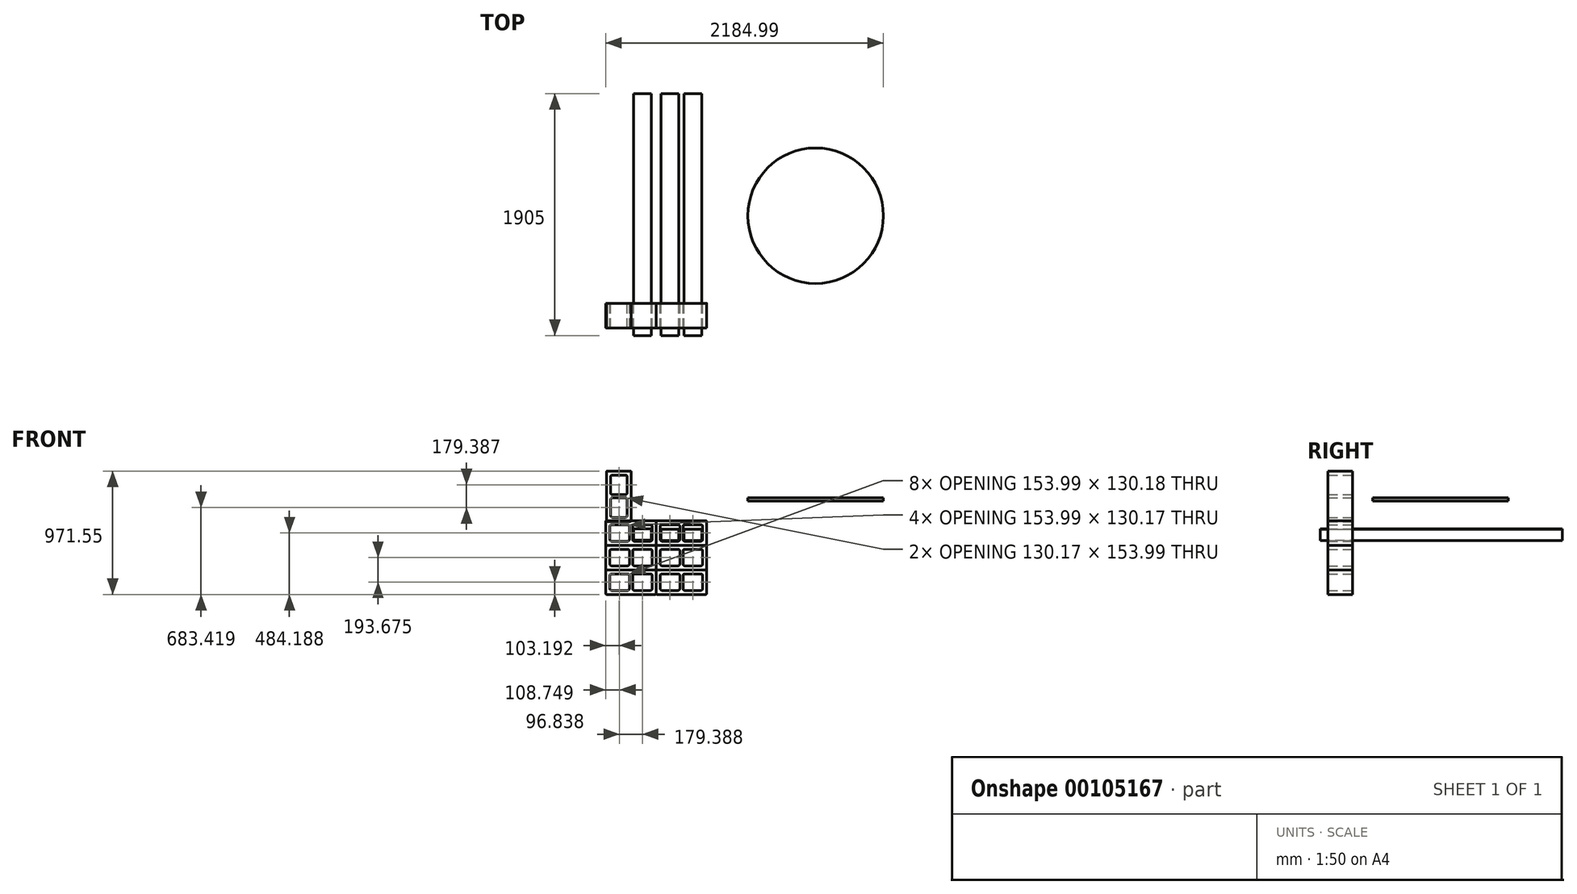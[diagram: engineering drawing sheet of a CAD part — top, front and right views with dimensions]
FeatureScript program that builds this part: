
annotation { "Feature Type Name" : "Feature", "Feature Type Description" : "" }
export const myFeature = defineFeature(function(context is Context, id is Id, definition is map)
    precondition{}
    {
        {
            var Q0;
            Q0=qCreatedBy(makeId("Front.planeOp"),FACE);
            var sketch = newSketch(context, id + "F0", { "sketchPlane" : qUnion([Q0])});
            skLineSegment(sketch, "E0.bottom", {"start": v(-6.35, 0) * mm, "end": v(-390.53, 0) * mm});
            skLineSegment(sketch, "E0.top", {"start": v(-6.35, 193.68) * mm, "end": v(-390.53, 193.67) * mm});
            skLineSegment(sketch, "E0.left", {"start": v(0, 6.35) * mm, "end": v(0, 187.32) * mm});
            skLineSegment(sketch, "E0.right", {"start": v(-396.88, 6.35) * mm, "end": v(-396.88, 187.32) * mm});
            skLineSegment(sketch, "E1.bottom", {"start": v(-352.43, 161.92) * mm, "end": v(-223.84, 161.92) * mm});
            skLineSegment(sketch, "E1.top", {"start": v(-352.43, 31.75) * mm, "end": v(-223.84, 31.75) * mm});
            skLineSegment(sketch, "E1.left", {"start": v(-365.13, 149.22) * mm, "end": v(-365.13, 44.45) * mm});
            skLineSegment(sketch, "E1.right", {"start": v(-211.14, 149.23) * mm, "end": v(-211.14, 44.45) * mm});
            skLineSegment(sketch, "E2.bottom", {"start": v(-173.04, 161.93) * mm, "end": v(-44.45, 161.93) * mm});
            skLineSegment(sketch, "E2.top", {"start": v(-173.04, 31.75) * mm, "end": v(-44.45, 31.75) * mm});
            skLineSegment(sketch, "E2.left", {"start": v(-185.74, 149.23) * mm, "end": v(-185.74, 44.45) * mm});
            skLineSegment(sketch, "E2.right", {"start": v(-31.75, 149.23) * mm, "end": v(-31.75, 44.45) * mm});
            skPoint(sketch, "E3.visualSharp", {"position": v(-396.88, 193.67) * mm});
            skArc(sketch, "E3.filletArc", {"start": v(-390.53, 193.67) * mm, "mid": v(-395.02, 191.82) * mm, "end": v(-396.88, 187.32) * mm});
            skPoint(sketch, "E4.visualSharp", {"position": v(-396.88, 0) * mm});
            skArc(sketch, "E4.filletArc", {"start": v(-396.88, 6.35) * mm, "mid": v(-395.02, 1.86) * mm, "end": v(-390.53, 0) * mm});
            skPoint(sketch, "E5.visualSharp", {"position": v(0, 0) * mm});
            skArc(sketch, "E5.filletArc", {"start": v(-6.35, 0) * mm, "mid": v(-1.86, 1.86) * mm, "end": v(0, 6.35) * mm});
            skPoint(sketch, "E6.visualSharp", {"position": v(0, 193.68) * mm});
            skArc(sketch, "E6.filletArc", {"start": v(0, 187.32) * mm, "mid": v(-1.86, 191.82) * mm, "end": v(-6.35, 193.67) * mm});
            skPoint(sketch, "E7.visualSharp", {"position": v(-365.13, 161.92) * mm});
            skArc(sketch, "E7.filletArc", {"start": v(-352.43, 161.92) * mm, "mid": v(-361.4, 158.2) * mm, "end": v(-365.13, 149.22) * mm});
            skPoint(sketch, "E8.visualSharp", {"position": v(-365.13, 31.75) * mm});
            skArc(sketch, "E8.filletArc", {"start": v(-365.13, 44.45) * mm, "mid": v(-361.4, 35.47) * mm, "end": v(-352.43, 31.75) * mm});
            skPoint(sketch, "E9.visualSharp", {"position": v(-211.14, 31.75) * mm});
            skArc(sketch, "E9.filletArc", {"start": v(-223.84, 31.75) * mm, "mid": v(-214.86, 35.47) * mm, "end": v(-211.14, 44.45) * mm});
            skPoint(sketch, "E10.visualSharp", {"position": v(-211.14, 161.92) * mm});
            skArc(sketch, "E10.filletArc", {"start": v(-211.14, 149.23) * mm, "mid": v(-214.86, 158.2) * mm, "end": v(-223.84, 161.93) * mm});
            skPoint(sketch, "E11.visualSharp", {"position": v(-185.74, 161.93) * mm});
            skArc(sketch, "E11.filletArc", {"start": v(-173.04, 161.93) * mm, "mid": v(-182.02, 158.2) * mm, "end": v(-185.74, 149.23) * mm});
            skPoint(sketch, "E12.visualSharp", {"position": v(-185.74, 31.75) * mm});
            skArc(sketch, "E12.filletArc", {"start": v(-185.74, 44.45) * mm, "mid": v(-182.02, 35.47) * mm, "end": v(-173.04, 31.75) * mm});
            skPoint(sketch, "E13.visualSharp", {"position": v(-31.75, 31.75) * mm});
            skArc(sketch, "E13.filletArc", {"start": v(-44.45, 31.75) * mm, "mid": v(-35.47, 35.47) * mm, "end": v(-31.75, 44.45) * mm});
            skPoint(sketch, "E14.visualSharp", {"position": v(-31.75, 161.93) * mm});
            skArc(sketch, "E14.filletArc", {"start": v(-31.75, 149.23) * mm, "mid": v(-35.47, 158.2) * mm, "end": v(-44.45, 161.93) * mm});
            skSolve(sketch);
        }
        {
            var Q0;
            Q0=qCreatedBy(makeId("Top.planeOp"),FACE);
            cPlane(context, id + "F1", {"entities" : qUnion([Q0]), "cplaneType" : CPlaneType.OFFSET, "offset" : 736.6 * mm, "width" : 152.4 * mm, "height" : 152.4 * mm});
        }
        {
            var Q0;
            Q0 = qSketchRegion(id + "F0", true);
            extrude(context, id + "F2", {"entities" : qUnion([Q0]), "depth" : 193.67 * mm});
        }
        {
            var Q0;
            Q0=makeQuery(id+"F2.opExtrude","SWEPT_BODY",BODY,{"disambiguationData":[OSD([sQuery(id+"F0.wireOp",EDGE,"E0.bottom"),sQuery(id+"F0.wireOp",EDGE,"E0.top"),sQuery(id+"F0.wireOp",EDGE,"E0.left"),sQuery(id+"F0.wireOp",EDGE,"E0.right"),sQuery(id+"F0.wireOp",EDGE,"E1.bottom"),sQuery(id+"F0.wireOp",EDGE,"E1.top"),sQuery(id+"F0.wireOp",EDGE,"E1.left"),sQuery(id+"F0.wireOp",EDGE,"E1.right"),sQuery(id+"F0.wireOp",EDGE,"E2.bottom"),sQuery(id+"F0.wireOp",EDGE,"E2.top"),sQuery(id+"F0.wireOp",EDGE,"E2.left"),sQuery(id+"F0.wireOp",EDGE,"E2.right"),sQuery(id+"F0.wireOp",EDGE,"E3.filletArc"),sQuery(id+"F0.wireOp",EDGE,"E4.filletArc"),sQuery(id+"F0.wireOp",EDGE,"E5.filletArc"),sQuery(id+"F0.wireOp",EDGE,"E6.filletArc"),sQuery(id+"F0.wireOp",EDGE,"E7.filletArc"),sQuery(id+"F0.wireOp",EDGE,"E8.filletArc"),sQuery(id+"F0.wireOp",EDGE,"E9.filletArc"),sQuery(id+"F0.wireOp",EDGE,"E10.filletArc"),sQuery(id+"F0.wireOp",EDGE,"E11.filletArc"),sQuery(id+"F0.wireOp",EDGE,"E12.filletArc"),sQuery(id+"F0.wireOp",EDGE,"E13.filletArc"),sQuery(id+"F0.wireOp",EDGE,"E14.filletArc")])]});
            transform(context, id + "F3", {"entities" : qUnion([Q0]), "transformType" : TransformType.TRANSLATION_3D, "dx" : 396.88 * mm, "dy" : 0 * mm, "dz" : 0 * mm, "makeCopy" : true});
        }
        {
            var Q0;
            Q0=qCreatedBy(id+"F1.planeOp",FACE);
            var sketch = newSketch(context, id + "F4", { "sketchPlane" : qUnion([Q0])});
            skCircle(sketch, "E15", {"center": v(1254.71, 689.64) * mm, "radius": 533.4 * mm});
            skSolve(sketch);
        }
        {
            var Q0;
            Q0=makeQuery(id+"F2.opExtrude","SWEPT_BODY",BODY,{"disambiguationData":[OSD([sQuery(id+"F0.wireOp",EDGE,"E0.bottom"),sQuery(id+"F0.wireOp",EDGE,"E0.top"),sQuery(id+"F0.wireOp",EDGE,"E0.left"),sQuery(id+"F0.wireOp",EDGE,"E0.right"),sQuery(id+"F0.wireOp",EDGE,"E1.bottom"),sQuery(id+"F0.wireOp",EDGE,"E1.top"),sQuery(id+"F0.wireOp",EDGE,"E1.left"),sQuery(id+"F0.wireOp",EDGE,"E1.right"),sQuery(id+"F0.wireOp",EDGE,"E2.bottom"),sQuery(id+"F0.wireOp",EDGE,"E2.top"),sQuery(id+"F0.wireOp",EDGE,"E2.left"),sQuery(id+"F0.wireOp",EDGE,"E2.right"),sQuery(id+"F0.wireOp",EDGE,"E3.filletArc"),sQuery(id+"F0.wireOp",EDGE,"E4.filletArc"),sQuery(id+"F0.wireOp",EDGE,"E5.filletArc"),sQuery(id+"F0.wireOp",EDGE,"E6.filletArc"),sQuery(id+"F0.wireOp",EDGE,"E7.filletArc"),sQuery(id+"F0.wireOp",EDGE,"E8.filletArc"),sQuery(id+"F0.wireOp",EDGE,"E9.filletArc"),sQuery(id+"F0.wireOp",EDGE,"E10.filletArc"),sQuery(id+"F0.wireOp",EDGE,"E11.filletArc"),sQuery(id+"F0.wireOp",EDGE,"E12.filletArc"),sQuery(id+"F0.wireOp",EDGE,"E13.filletArc"),sQuery(id+"F0.wireOp",EDGE,"E14.filletArc")])]});
            transform(context, id + "F5", {"entities" : qUnion([Q0]), "transformType" : TransformType.TRANSLATION_3D, "dx" : 0 * mm, "dy" : 0 * mm, "dz" : 193.67 * mm, "makeCopy" : true});
        }
        {
            var Q0;
            Q0=makeQuery(id+"F3.opPattern","COPY",BODY,{"derivedFrom":makeQuery(id+"F2.opExtrude","SWEPT_BODY",BODY,{"disambiguationData":[OSD([sQuery(id+"F0.wireOp",EDGE,"E0.bottom"),sQuery(id+"F0.wireOp",EDGE,"E0.top"),sQuery(id+"F0.wireOp",EDGE,"E0.left"),sQuery(id+"F0.wireOp",EDGE,"E0.right"),sQuery(id+"F0.wireOp",EDGE,"E1.bottom"),sQuery(id+"F0.wireOp",EDGE,"E1.top"),sQuery(id+"F0.wireOp",EDGE,"E1.left"),sQuery(id+"F0.wireOp",EDGE,"E1.right"),sQuery(id+"F0.wireOp",EDGE,"E2.bottom"),sQuery(id+"F0.wireOp",EDGE,"E2.top"),sQuery(id+"F0.wireOp",EDGE,"E2.left"),sQuery(id+"F0.wireOp",EDGE,"E2.right"),sQuery(id+"F0.wireOp",EDGE,"E3.filletArc"),sQuery(id+"F0.wireOp",EDGE,"E4.filletArc"),sQuery(id+"F0.wireOp",EDGE,"E5.filletArc"),sQuery(id+"F0.wireOp",EDGE,"E6.filletArc"),sQuery(id+"F0.wireOp",EDGE,"E7.filletArc"),sQuery(id+"F0.wireOp",EDGE,"E8.filletArc"),sQuery(id+"F0.wireOp",EDGE,"E9.filletArc"),sQuery(id+"F0.wireOp",EDGE,"E10.filletArc"),sQuery(id+"F0.wireOp",EDGE,"E11.filletArc"),sQuery(id+"F0.wireOp",EDGE,"E12.filletArc"),sQuery(id+"F0.wireOp",EDGE,"E13.filletArc"),sQuery(id+"F0.wireOp",EDGE,"E14.filletArc")])]}),"instanceName":"1"});
            transform(context, id + "F6", {"entities" : qUnion([Q0]), "transformType" : TransformType.TRANSLATION_3D, "dx" : 0 * mm, "dy" : 0 * mm, "dz" : 193.67 * mm, "makeCopy" : true});
        }
        {
            var Q0;
            Q0=makeQuery(id+"F5.opPattern","COPY",BODY,{"derivedFrom":makeQuery(id+"F2.opExtrude","SWEPT_BODY",BODY,{"disambiguationData":[OSD([sQuery(id+"F0.wireOp",EDGE,"E0.bottom"),sQuery(id+"F0.wireOp",EDGE,"E0.top"),sQuery(id+"F0.wireOp",EDGE,"E0.left"),sQuery(id+"F0.wireOp",EDGE,"E0.right"),sQuery(id+"F0.wireOp",EDGE,"E1.bottom"),sQuery(id+"F0.wireOp",EDGE,"E1.top"),sQuery(id+"F0.wireOp",EDGE,"E1.left"),sQuery(id+"F0.wireOp",EDGE,"E1.right"),sQuery(id+"F0.wireOp",EDGE,"E2.bottom"),sQuery(id+"F0.wireOp",EDGE,"E2.top"),sQuery(id+"F0.wireOp",EDGE,"E2.left"),sQuery(id+"F0.wireOp",EDGE,"E2.right"),sQuery(id+"F0.wireOp",EDGE,"E3.filletArc"),sQuery(id+"F0.wireOp",EDGE,"E4.filletArc"),sQuery(id+"F0.wireOp",EDGE,"E5.filletArc"),sQuery(id+"F0.wireOp",EDGE,"E6.filletArc"),sQuery(id+"F0.wireOp",EDGE,"E7.filletArc"),sQuery(id+"F0.wireOp",EDGE,"E8.filletArc"),sQuery(id+"F0.wireOp",EDGE,"E9.filletArc"),sQuery(id+"F0.wireOp",EDGE,"E10.filletArc"),sQuery(id+"F0.wireOp",EDGE,"E11.filletArc"),sQuery(id+"F0.wireOp",EDGE,"E12.filletArc"),sQuery(id+"F0.wireOp",EDGE,"E13.filletArc"),sQuery(id+"F0.wireOp",EDGE,"E14.filletArc")])]}),"instanceName":"1"});
            transform(context, id + "F7", {"entities" : qUnion([Q0]), "transformType" : TransformType.TRANSLATION_3D, "dx" : 0 * mm, "dy" : 0 * mm, "dz" : 193.67 * mm, "makeCopy" : true});
        }
        {
            var Q0;
            Q0=makeQuery(id+"F6.opPattern","COPY",BODY,{"derivedFrom":makeQuery(id+"F3.opPattern","COPY",BODY,{"derivedFrom":makeQuery(id+"F2.opExtrude","SWEPT_BODY",BODY,{"disambiguationData":[OSD([sQuery(id+"F0.wireOp",EDGE,"E0.bottom"),sQuery(id+"F0.wireOp",EDGE,"E0.top"),sQuery(id+"F0.wireOp",EDGE,"E0.left"),sQuery(id+"F0.wireOp",EDGE,"E0.right"),sQuery(id+"F0.wireOp",EDGE,"E1.bottom"),sQuery(id+"F0.wireOp",EDGE,"E1.top"),sQuery(id+"F0.wireOp",EDGE,"E1.left"),sQuery(id+"F0.wireOp",EDGE,"E1.right"),sQuery(id+"F0.wireOp",EDGE,"E2.bottom"),sQuery(id+"F0.wireOp",EDGE,"E2.top"),sQuery(id+"F0.wireOp",EDGE,"E2.left"),sQuery(id+"F0.wireOp",EDGE,"E2.right"),sQuery(id+"F0.wireOp",EDGE,"E3.filletArc"),sQuery(id+"F0.wireOp",EDGE,"E4.filletArc"),sQuery(id+"F0.wireOp",EDGE,"E5.filletArc"),sQuery(id+"F0.wireOp",EDGE,"E6.filletArc"),sQuery(id+"F0.wireOp",EDGE,"E7.filletArc"),sQuery(id+"F0.wireOp",EDGE,"E8.filletArc"),sQuery(id+"F0.wireOp",EDGE,"E9.filletArc"),sQuery(id+"F0.wireOp",EDGE,"E10.filletArc"),sQuery(id+"F0.wireOp",EDGE,"E11.filletArc"),sQuery(id+"F0.wireOp",EDGE,"E12.filletArc"),sQuery(id+"F0.wireOp",EDGE,"E13.filletArc"),sQuery(id+"F0.wireOp",EDGE,"E14.filletArc")])]}),"instanceName":"1"}),"instanceName":"1"});
            transform(context, id + "F8", {"entities" : qUnion([Q0]), "transformType" : TransformType.TRANSLATION_3D, "dx" : 0 * mm, "dy" : 0 * mm, "dz" : 193.67 * mm, "makeCopy" : true});
        }
        {
            var Q0;
            Q0=qCreatedBy(makeId("Front.planeOp"),FACE);
            var sketch = newSketch(context, id + "F9", { "sketchPlane" : qUnion([Q0])});
            skLineSegment(sketch, "E16.bottom", {"start": v(-39.23, 425.97) * mm, "end": v(-178.93, 425.97) * mm});
            skLineSegment(sketch, "E16.top", {"start": v(-39.23, 514.87) * mm, "end": v(-178.93, 514.87) * mm});
            skLineSegment(sketch, "E16.left", {"start": v(-39.23, 425.97) * mm, "end": v(-39.23, 514.87) * mm});
            skLineSegment(sketch, "E16.right", {"start": v(-178.93, 425.97) * mm, "end": v(-178.93, 514.87) * mm});
            skLineSegment(sketch, "E17.bottom", {"start": v(38.16, 513.85) * mm, "end": v(177.86, 513.85) * mm});
            skLineSegment(sketch, "E17.top", {"start": v(38.16, 424.95) * mm, "end": v(177.86, 424.95) * mm});
            skLineSegment(sketch, "E17.left", {"start": v(38.16, 513.85) * mm, "end": v(38.16, 424.95) * mm});
            skLineSegment(sketch, "E17.right", {"start": v(177.86, 513.85) * mm, "end": v(177.86, 424.95) * mm});
            skLineSegment(sketch, "E18.bottom", {"start": v(218.4, 514.16) * mm, "end": v(358.1, 514.16) * mm});
            skLineSegment(sketch, "E18.top", {"start": v(218.4, 425.26) * mm, "end": v(358.1, 425.26) * mm});
            skLineSegment(sketch, "E18.left", {"start": v(218.4, 514.16) * mm, "end": v(218.4, 425.26) * mm});
            skLineSegment(sketch, "E18.right", {"start": v(358.1, 514.16) * mm, "end": v(358.1, 425.26) * mm});
            skSolve(sketch);
        }
        {
            var Q0;
            Q0 = qSketchRegion(id + "F9", true);
            extrude(context, id + "F10", {"entities" : qUnion([Q0]), "depth" : 254 * mm, "hasSecondDirection" : true, "secondDirectionOppositeDirection" : true, "secondDirectionDepth" : 1651 * mm});
        }
        {
            var Q0;
            Q0=makeQuery(id+"F4.imprint","IMPRINT",FACE,{"disambiguationData":[TD([[makeQuery(id+"F4.imprint","IMPRINT",EDGE,{"derivedFrom":sQuery(id+"F4.wireOp",EDGE,"E15")}),1.0]])]});
            extrude(context, id + "F11", {"entities" : qUnion([Q0]), "depth" : 25.4 * mm});
        }
        {
            var Q0;
            Q0=makeQuery(id+"F7.opPattern","COPY",BODY,{"derivedFrom":makeQuery(id+"F5.opPattern","COPY",BODY,{"derivedFrom":makeQuery(id+"F2.opExtrude","SWEPT_BODY",BODY,{"disambiguationData":[OSD([sQuery(id+"F0.wireOp",EDGE,"E0.bottom"),sQuery(id+"F0.wireOp",EDGE,"E0.top"),sQuery(id+"F0.wireOp",EDGE,"E0.left"),sQuery(id+"F0.wireOp",EDGE,"E0.right"),sQuery(id+"F0.wireOp",EDGE,"E1.bottom"),sQuery(id+"F0.wireOp",EDGE,"E1.top"),sQuery(id+"F0.wireOp",EDGE,"E1.left"),sQuery(id+"F0.wireOp",EDGE,"E1.right"),sQuery(id+"F0.wireOp",EDGE,"E2.bottom"),sQuery(id+"F0.wireOp",EDGE,"E2.top"),sQuery(id+"F0.wireOp",EDGE,"E2.left"),sQuery(id+"F0.wireOp",EDGE,"E2.right"),sQuery(id+"F0.wireOp",EDGE,"E3.filletArc"),sQuery(id+"F0.wireOp",EDGE,"E4.filletArc"),sQuery(id+"F0.wireOp",EDGE,"E5.filletArc"),sQuery(id+"F0.wireOp",EDGE,"E6.filletArc"),sQuery(id+"F0.wireOp",EDGE,"E7.filletArc"),sQuery(id+"F0.wireOp",EDGE,"E8.filletArc"),sQuery(id+"F0.wireOp",EDGE,"E9.filletArc"),sQuery(id+"F0.wireOp",EDGE,"E10.filletArc"),sQuery(id+"F0.wireOp",EDGE,"E11.filletArc"),sQuery(id+"F0.wireOp",EDGE,"E12.filletArc"),sQuery(id+"F0.wireOp",EDGE,"E13.filletArc"),sQuery(id+"F0.wireOp",EDGE,"E14.filletArc")])]}),"instanceName":"1"}),"instanceName":"1"});
            var Q1;
            Q1=makeQuery(id+"F7.opPattern","COPY",EDGE,{"derivedFrom":makeQuery(id+"F5.opPattern","COPY",EDGE,{"derivedFrom":makeQuery(id+"F2.opExtrude","SWEPT_EDGE",EDGE,{"disambiguationData":[OSD([sQuery(id+"F0.wireOp",EDGE,"E0.top"),sQuery(id+"F0.wireOp",EDGE,"E3.filletArc")])]}),"instanceName":"1"}),"instanceName":"1"});
            transform(context, id + "F12", {"entities" : qUnion([Q0]), "transformType" : TransformType.ROTATION, "transformAxis" : qUnion([Q1]), "angle" : 90 * degree, "oppositeDirection" : true, "makeCopy" : true});
        }
    });
